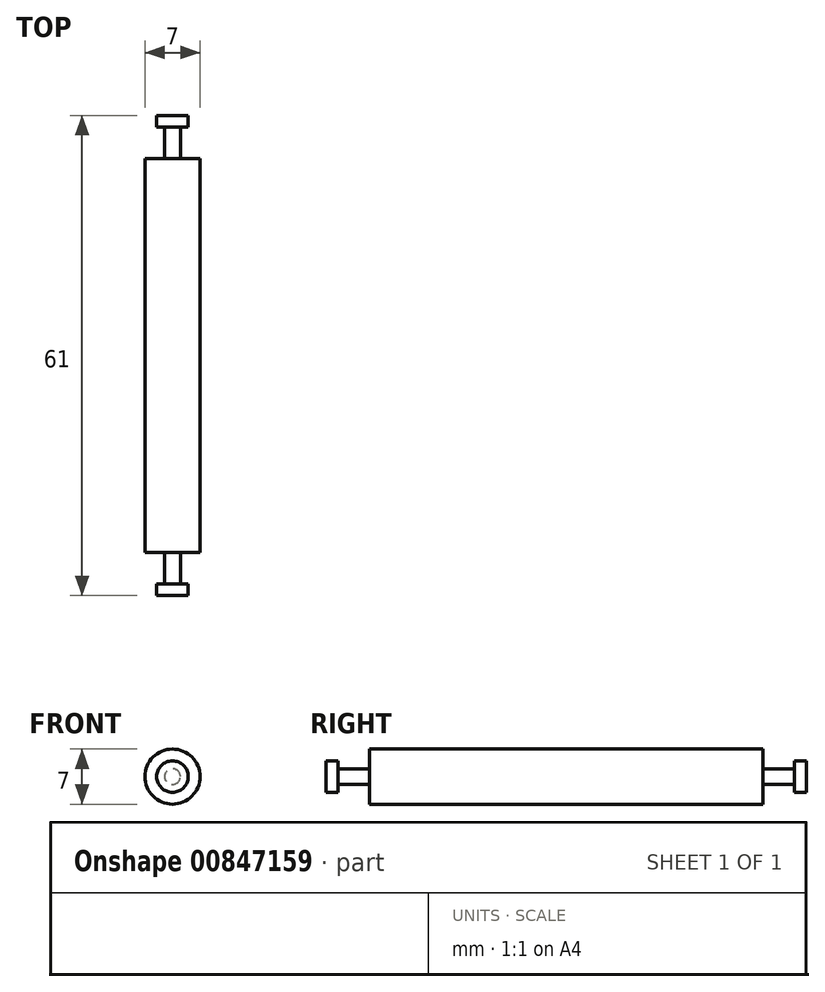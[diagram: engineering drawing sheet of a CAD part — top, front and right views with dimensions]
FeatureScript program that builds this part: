
annotation { "Feature Type Name" : "Feature", "Feature Type Description" : "" }
export const myFeature = defineFeature(function(context is Context, id is Id, definition is map)
    precondition{}
    {
        {
            var Q0;
            Q0=qCreatedBy(makeId("Front.planeOp"),FACE);
            var sketch = newSketch(context, id + "F0", { "sketchPlane" : qUnion([Q0])});
            skCircle(sketch, "E0", {"center": v(0, 0) * mm, "radius": 1 * mm});
            skCircle(sketch, "E1", {"center": v(0, 0) * mm, "radius": 2 * mm});
            skCircle(sketch, "E2", {"center": v(0, 0) * mm, "radius": 3.5 * mm});
            skSolve(sketch);
        }
        {
            var Q0;
            Q0=makeQuery(id+"F0.imprint","IMPRINT",FACE,{"disambiguationData":[TD([[makeQuery(id+"F0.imprint","IMPRINT",EDGE,{"derivedFrom":sQuery(id+"F0.wireOp",EDGE,"E1")}),-1.0]])]});
            var Q1;
            Q1=makeQuery(id+"F0.imprint","IMPRINT",FACE,{"disambiguationData":[TD([[makeQuery(id+"F0.imprint","IMPRINT",EDGE,{"derivedFrom":sQuery(id+"F0.wireOp",EDGE,"E0")}),1.0]])]});
            var Q2;
            Q2=makeQuery(id+"F0.imprint","IMPRINT",FACE,{"disambiguationData":[TD([[makeQuery(id+"F0.imprint","IMPRINT",EDGE,{"derivedFrom":sQuery(id+"F0.wireOp",EDGE,"E0")}),-1.0]])]});
            extrude(context, id + "F1", {"entities" : qUnion([Q0, Q1, Q2]), "oppositeDirection" : true, "depth" : 25 * mm, "offsetDistance" : 25 * mm});
        }
        {
            var Q0;
            Q0=qCreatedBy(makeId("Front.planeOp"),FACE);
            var sketch = newSketch(context, id + "F2", { "sketchPlane" : qUnion([Q0])});
            skCircle(sketch, "E3", {"center": v(0, 0) * mm, "radius": 1 * mm});
            skSolve(sketch);
        }
        {
            var Q0;
            Q0 = qSketchRegion(id + "F2", true);
            extrude(context, id + "F3", {"entities" : qUnion([Q0]), "operationType" : NewBodyOperationType.ADD, "depth" : 4 * mm, "offsetDistance" : 25 * mm});
        }
        {
            var Q0;
            Q0=qCreatedBy(makeId("Right.planeOp"),FACE);
            var sketch = newSketch(context, id + "F4", { "sketchPlane" : qUnion([Q0])});
            skLineSegment(sketch, "E4.bottom", {"start": v(-5.5, 2) * mm, "end": v(-4, 2) * mm});
            skLineSegment(sketch, "E4.top", {"start": v(-5.5, 0) * mm, "end": v(-4, 0) * mm});
            skLineSegment(sketch, "E4.left", {"start": v(-5.5, 2) * mm, "end": v(-5.5, 0) * mm});
            skLineSegment(sketch, "E4.right", {"start": v(-4, 2) * mm, "end": v(-4, 0) * mm});
            skSolve(sketch);
        }
        {
            var Q0;
            Q0=makeQuery(id+"F4.imprint","IMPRINT",FACE,{"disambiguationData":[TD([[makeQuery(id+"F4.imprint","IMPRINT",EDGE,{"derivedFrom":sQuery(id+"F4.wireOp",EDGE,"E4.bottom")}),-1.0]])]});
            var Q1;
            Q1=sQuery(id+"F4.wireOp",EDGE,"E4.top");
            revolve(context, id + "F5", {"operationType" : NewBodyOperationType.ADD, "surfaceOperationType" : NewSurfaceOperationType.NEW, "entities" : qUnion([Q0]), "axis" : qUnion([Q1]), "revolveType" : RevolveType.FULL});
        }
        {
            var Q0;
            Q0=makeQuery(id+"F1.opExtrude","SWEPT_BODY",BODY,{"disambiguationData":[OSD([sQuery(id+"F0.wireOp",EDGE,"E2")])]});
            var Q1;
            Q1=makeQuery(id+"F1.opExtrude","CAP_FACE",FACE,{"disambiguationData":[OSD([sQuery(id+"F0.wireOp",EDGE,"E2")])],"isStart":false});
            mirror(context, id + "F6", {"operationType" : NewBodyOperationType.ADD, "entities" : qUnion([Q0]), "mirrorPlane" : qUnion([Q1])});
        }
    });
